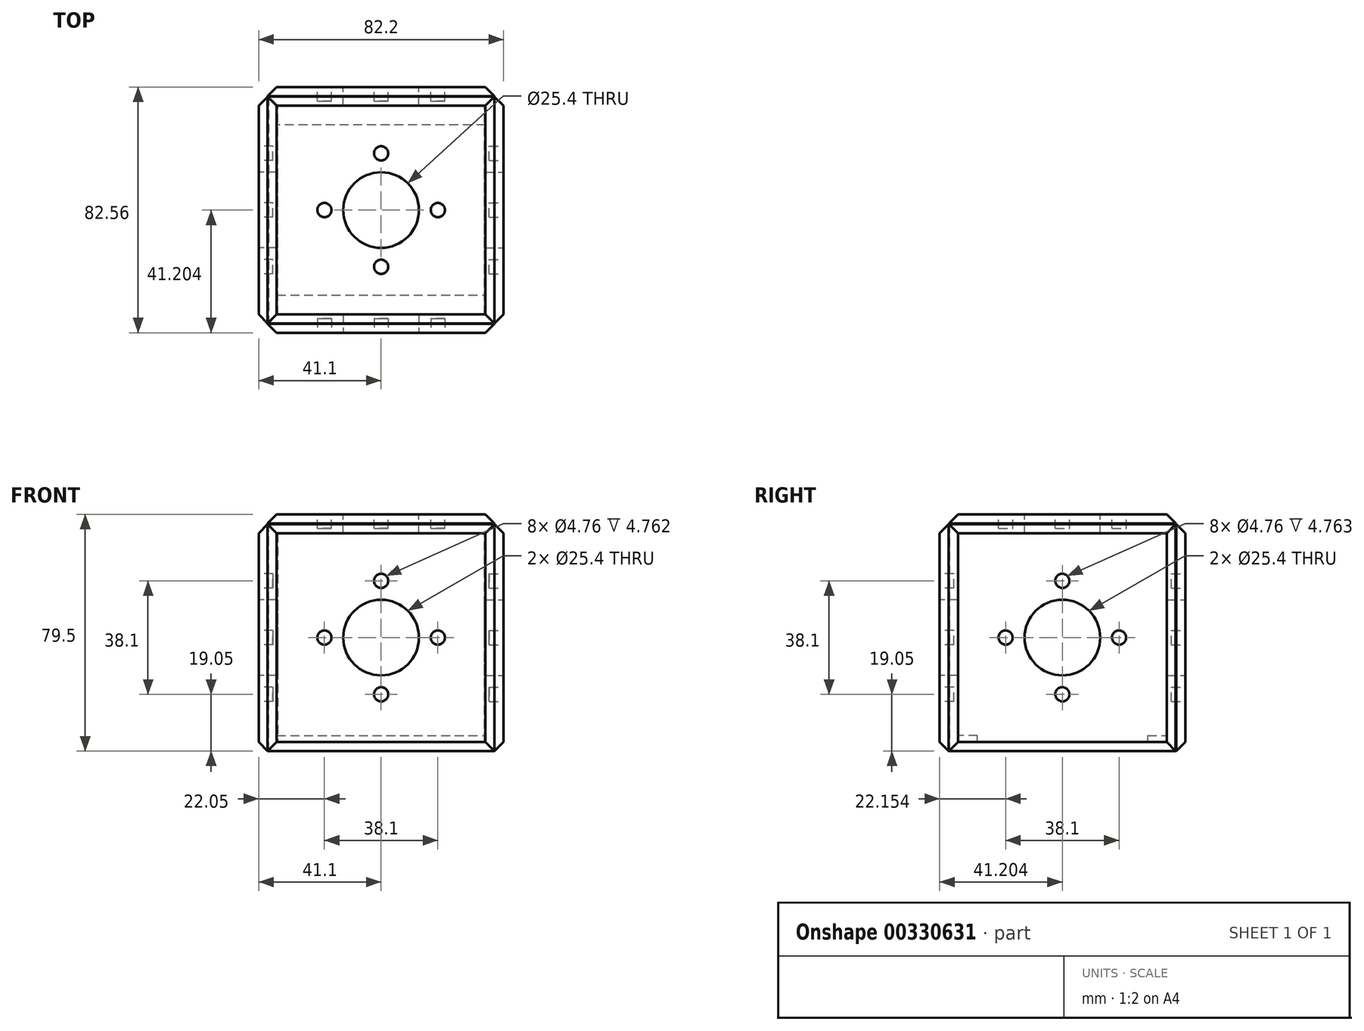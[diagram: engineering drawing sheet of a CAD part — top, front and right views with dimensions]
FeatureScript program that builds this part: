
annotation { "Feature Type Name" : "Feature", "Feature Type Description" : "" }
export const myFeature = defineFeature(function(context is Context, id is Id, definition is map)
    precondition{}
    {
        {
            var Q0;
            Q0=qCreatedBy(makeId("Front.planeOp"),FACE);
            var sketch = newSketch(context, id + "F0", { "sketchPlane" : qUnion([Q0])});
            skLineSegment(sketch, "E0.bottom", {"start": v(-38.1, 38.1) * mm, "end": v(38.1, 38.1) * mm});
            skLineSegment(sketch, "E0.top", {"start": v(-38.1, -38.1) * mm, "end": v(38.1, -38.1) * mm});
            skLineSegment(sketch, "E0.left", {"start": v(-38.1, 38.1) * mm, "end": v(-38.1, -38.1) * mm});
            skLineSegment(sketch, "E0.right", {"start": v(38.1, 38.1) * mm, "end": v(38.1, -38.1) * mm});
            skPoint(sketch, "E0.middle", {"position": v(0, 0) * mm});
            skSolve(sketch);
        }
        {
            var Q0;
            Q0=makeQuery(id+"F0.imprint","IMPRINT",FACE,{"disambiguationData":[TD([[makeQuery(id+"F0.imprint","IMPRINT",EDGE,{"derivedFrom":sQuery(id+"F0.wireOp",EDGE,"E0.bottom")}),-1.0]])]});
            extrude(context, id + "F1", {"entities" : qUnion([Q0]), "depth" : 6.35 * mm});
        }
        {
            var Q0;
            Q0=makeQuery(id+"F1.opExtrude","CAP_EDGE",EDGE,{"disambiguationData":[OSD([sQuery(id+"F0.wireOp",EDGE,"E0.bottom")])],"isStart":false});
            var Q1;
            Q1=makeQuery(id+"F1.opExtrude","CAP_EDGE",EDGE,{"disambiguationData":[OSD([sQuery(id+"F0.wireOp",EDGE,"E0.bottom")])],"isStart":true});
            var Q2;
            Q2=makeQuery(id+"F1.opExtrude","CAP_EDGE",EDGE,{"disambiguationData":[OSD([sQuery(id+"F0.wireOp",EDGE,"E0.left")])],"isStart":false});
            var Q3;
            Q3=makeQuery(id+"F1.opExtrude","CAP_EDGE",EDGE,{"disambiguationData":[OSD([sQuery(id+"F0.wireOp",EDGE,"E0.left")])],"isStart":true});
            var Q4;
            Q4=makeQuery(id+"F1.opExtrude","CAP_EDGE",EDGE,{"disambiguationData":[OSD([sQuery(id+"F0.wireOp",EDGE,"E0.top")])],"isStart":false});
            var Q5;
            Q5=makeQuery(id+"F1.opExtrude","CAP_EDGE",EDGE,{"disambiguationData":[OSD([sQuery(id+"F0.wireOp",EDGE,"E0.top")])],"isStart":true});
            var Q6;
            Q6=makeQuery(id+"F1.opExtrude","CAP_EDGE",EDGE,{"disambiguationData":[OSD([sQuery(id+"F0.wireOp",EDGE,"E0.right")])],"isStart":false});
            var Q7;
            Q7=makeQuery(id+"F1.opExtrude","CAP_EDGE",EDGE,{"disambiguationData":[OSD([sQuery(id+"F0.wireOp",EDGE,"E0.right")])],"isStart":true});
            chamfer(context, id + "F2", {"entities" : qUnion([Q0, Q1, Q2, Q3, Q4, Q5, Q6, Q7]), "chamferType" : ChamferType.OFFSET_ANGLE, "width" : 3.05 * mm, "oppositeDirection" : false, "angle" : 45 * degree, "tangentPropagation" : true});
        }
        {
            var Q0;
            Q0=makeQuery(id+"F1.opExtrude","CAP_FACE",FACE,{"disambiguationData":[OSD([sQuery(id+"F0.wireOp",EDGE,"E0.bottom"),sQuery(id+"F0.wireOp",EDGE,"E0.top"),sQuery(id+"F0.wireOp",EDGE,"E0.left"),sQuery(id+"F0.wireOp",EDGE,"E0.right")])],"isStart":false});
            var sketch = newSketch(context, id + "F3", { "sketchPlane" : qUnion([Q0])});
            skCircle(sketch, "E1", {"center": v(0, 0) * mm, "radius": 12.7 * mm});
            skSolve(sketch);
        }
        {
            var Q0;
            Q0=makeQuery(id+"F3.imprint","IMPRINT",FACE,{"disambiguationData":[TD([[makeQuery(id+"F3.imprint","IMPRINT",EDGE,{"derivedFrom":sQuery(id+"F3.wireOp",EDGE,"E1")}),1.0]])]});
            extrude(context, id + "F4", {"entities" : qUnion([Q0]), "operationType" : NewBodyOperationType.REMOVE, "oppositeDirection" : true, "depth" : 6.35 * mm});
        }
        {
            var Q0;
            Q0=makeQuery(id+"F1.opExtrude","CAP_FACE",FACE,{"disambiguationData":[OSD([sQuery(id+"F0.wireOp",EDGE,"E0.bottom"),sQuery(id+"F0.wireOp",EDGE,"E0.top"),sQuery(id+"F0.wireOp",EDGE,"E0.left"),sQuery(id+"F0.wireOp",EDGE,"E0.right")])],"isStart":false});
            var sketch = newSketch(context, id + "F5", { "sketchPlane" : qUnion([Q0])});
            skCircle(sketch, "E2", {"center": v(0, 19.05) * mm, "radius": 2.38 * mm});
            skCircle(sketch, "E3.1.0", {"center": v(19.05, 0) * mm, "radius": 2.38 * mm});
            skCircle(sketch, "E3.2.0", {"center": v(0, -19.05) * mm, "radius": 2.38 * mm});
            skCircle(sketch, "E3.3.0", {"center": v(-19.05, 0) * mm, "radius": 2.38 * mm});
            skPoint(sketch, "E3.center", {"position": v(0, 0) * mm});
            skLineSegment(sketch, "E3.anchor1", {"start": v(0, 0) * mm, "end": v(0, 19.05) * mm, "construction": true});
            skLineSegment(sketch, "E3.anchor2", {"start": v(0, 0) * mm, "end": v(-19.05, 0) * mm, "construction": true});
            skSolve(sketch);
        }
        {
            var Q0;
            Q0=makeQuery(id+"F5.imprint","IMPRINT",FACE,{"disambiguationData":[TD([[makeQuery(id+"F5.imprint","IMPRINT",EDGE,{"derivedFrom":sQuery(id+"F5.wireOp",EDGE,"E2")}),1.0]])]});
            var Q1;
            Q1=makeQuery(id+"F5.imprint","IMPRINT",FACE,{"disambiguationData":[TD([[makeQuery(id+"F5.imprint","IMPRINT",EDGE,{"derivedFrom":sQuery(id+"F5.wireOp",EDGE,"E3.1.0")}),1.0]])]});
            var Q2;
            Q2=makeQuery(id+"F5.imprint","IMPRINT",FACE,{"disambiguationData":[TD([[makeQuery(id+"F5.imprint","IMPRINT",EDGE,{"derivedFrom":sQuery(id+"F5.wireOp",EDGE,"E3.2.0")}),1.0]])]});
            var Q3;
            Q3=makeQuery(id+"F5.imprint","IMPRINT",FACE,{"disambiguationData":[TD([[makeQuery(id+"F5.imprint","IMPRINT",EDGE,{"derivedFrom":sQuery(id+"F5.wireOp",EDGE,"E3.3.0")}),1.0]])]});
            extrude(context, id + "F6", {"entities" : qUnion([Q0, Q1, Q2, Q3]), "operationType" : NewBodyOperationType.REMOVE, "oppositeDirection" : true, "depth" : 4.76 * mm});
        }
        {
            var Q0;
            Q0=makeQuery(id+"F1.opExtrude","SWEPT_BODY",BODY,{"disambiguationData":[OSD([sQuery(id+"F0.wireOp",EDGE,"E0.bottom"),sQuery(id+"F0.wireOp",EDGE,"E0.top"),sQuery(id+"F0.wireOp",EDGE,"E0.left"),sQuery(id+"F0.wireOp",EDGE,"E0.right")])]});
            transform(context, id + "F7", {"entities" : qUnion([Q0]), "transformType" : TransformType.TRANSLATION_3D, "dx" : 0 * mm, "dy" : -34.92 * mm, "dz" : 0 * mm, "makeCopy" : false});
        }
        {
            var Q0;
            Q0=makeQuery(id+"F1.opExtrude","SWEPT_BODY",BODY,{"disambiguationData":[OSD([sQuery(id+"F0.wireOp",EDGE,"E0.bottom"),sQuery(id+"F0.wireOp",EDGE,"E0.top"),sQuery(id+"F0.wireOp",EDGE,"E0.left"),sQuery(id+"F0.wireOp",EDGE,"E0.right")])]});
            var Q1;
            Q1=qCreatedBy(makeId("Front.planeOp"),FACE);
            mirror(context, id + "F8", {"entities" : qUnion([Q0]), "mirrorPlane" : qUnion([Q1])});
        }
        {
            var Q0;
            Q0=makeQuery(id+"F8.opPattern","COPY",FACE,{"derivedFrom":makeQuery(id+"F1.opExtrude","SWEPT_FACE",FACE,{"disambiguationData":[OSD([sQuery(id+"F0.wireOp",EDGE,"E0.bottom")])]}),"instanceName":"1"});
            cPlane(context, id + "F9", {"entities" : qUnion([Q0]), "cplaneType" : CPlaneType.OFFSET, "offset" : 1.78 * mm, "width" : 152.4 * mm, "height" : 152.4 * mm});
        }
        {
            var Q0;
            Q0=makeQuery(id+"F8.opPattern","COPY",BODY,{"derivedFrom":makeQuery(id+"F1.opExtrude","SWEPT_BODY",BODY,{"disambiguationData":[OSD([sQuery(id+"F0.wireOp",EDGE,"E0.bottom"),sQuery(id+"F0.wireOp",EDGE,"E0.top"),sQuery(id+"F0.wireOp",EDGE,"E0.left"),sQuery(id+"F0.wireOp",EDGE,"E0.right")])]}),"instanceName":"1"});
            var Q1;
            Q1=qCreatedBy(id+"F9.planeOp",FACE);
            mirror(context, id + "F10", {"operationType" : NewBodyOperationType.ADD, "entities" : qUnion([Q0]), "mirrorPlane" : qUnion([Q1])});
        }
        {
            var Q0;
            Q0=makeQuery(id+"F10.opPattern","COPY",BODY,{"derivedFrom":makeQuery(id+"F8.opPattern","COPY",BODY,{"derivedFrom":makeQuery(id+"F1.opExtrude","SWEPT_BODY",BODY,{"disambiguationData":[OSD([sQuery(id+"F0.wireOp",EDGE,"E0.bottom"),sQuery(id+"F0.wireOp",EDGE,"E0.top"),sQuery(id+"F0.wireOp",EDGE,"E0.left"),sQuery(id+"F0.wireOp",EDGE,"E0.right")])]}),"instanceName":"1"}),"instanceName":"1"});
            var Q1;
            {var subQ0=sQuery(id+"F0.wireOp",EDGE,"E0.bottom");Q1=makeQuery(id+"F8.opPattern","COPY",EDGE,{"derivedFrom":makeQuery(id+"F2.opChamfer","BLEND_EDGE",EDGE,{"blendedFrom":[makeQuery(id+"F1.opExtrude","CAP_EDGE",EDGE,{"disambiguationData":[OSD([subQ0])],"isStart":true}),makeQuery(id+"F1.opExtrude","SWEPT_FACE",FACE,{"disambiguationData":[OSD([subQ0])]})],"blendedInto":[makeQuery(id+"F1.opExtrude","SWEPT_FACE",FACE,{"disambiguationData":[OSD([subQ0])]})]}),"instanceName":"1"});}
            transform(context, id + "F11", {"entities" : qUnion([Q0]), "transformType" : TransformType.ROTATION, "transformAxis" : qUnion([Q1]), "angle" : 90 * degree, "oppositeDirection" : true, "makeCopy" : false});
        }
        {
            var Q0;
            Q0=makeQuery(id+"F10.opPattern","COPY",BODY,{"derivedFrom":makeQuery(id+"F8.opPattern","COPY",BODY,{"derivedFrom":makeQuery(id+"F1.opExtrude","SWEPT_BODY",BODY,{"disambiguationData":[OSD([sQuery(id+"F0.wireOp",EDGE,"E0.bottom"),sQuery(id+"F0.wireOp",EDGE,"E0.top"),sQuery(id+"F0.wireOp",EDGE,"E0.left"),sQuery(id+"F0.wireOp",EDGE,"E0.right")])]}),"instanceName":"1"}),"instanceName":"1"});
            transform(context, id + "F12", {"entities" : qUnion([Q0]), "transformType" : TransformType.TRANSLATION_3D, "dx" : 0 * mm, "dy" : 3.6 * mm, "dz" : 0 * mm, "makeCopy" : false});
        }
        {
            var Q0;
            Q0=makeQuery(id+"F10.opPattern","COPY",FACE,{"derivedFrom":makeQuery(id+"F8.opPattern","COPY",FACE,{"derivedFrom":makeQuery(id+"F1.opExtrude","SWEPT_FACE",FACE,{"disambiguationData":[OSD([sQuery(id+"F0.wireOp",EDGE,"E0.right")])]}),"instanceName":"1"}),"instanceName":"1"});
            cPlane(context, id + "F13", {"entities" : qUnion([Q0]), "cplaneType" : CPlaneType.OFFSET, "offset" : 0.36 * mm, "width" : 152.4 * mm, "height" : 152.4 * mm});
        }
        {
            var Q0;
            Q0=makeQuery(id+"F10.opPattern","COPY",BODY,{"derivedFrom":makeQuery(id+"F8.opPattern","COPY",BODY,{"derivedFrom":makeQuery(id+"F1.opExtrude","SWEPT_BODY",BODY,{"disambiguationData":[OSD([sQuery(id+"F0.wireOp",EDGE,"E0.bottom"),sQuery(id+"F0.wireOp",EDGE,"E0.top"),sQuery(id+"F0.wireOp",EDGE,"E0.left"),sQuery(id+"F0.wireOp",EDGE,"E0.right")])]}),"instanceName":"1"}),"instanceName":"1"});
            var Q1;
            Q1=qCreatedBy(id+"F13.planeOp",FACE);
            mirror(context, id + "F14", {"entities" : qUnion([Q0]), "mirrorPlane" : qUnion([Q1])});
        }
        {
            var Q0;
            Q0=makeQuery(id+"F14.opPattern","COPY",BODY,{"derivedFrom":makeQuery(id+"F10.opPattern","COPY",BODY,{"derivedFrom":makeQuery(id+"F8.opPattern","COPY",BODY,{"derivedFrom":makeQuery(id+"F1.opExtrude","SWEPT_BODY",BODY,{"disambiguationData":[OSD([sQuery(id+"F0.wireOp",EDGE,"E0.bottom"),sQuery(id+"F0.wireOp",EDGE,"E0.top"),sQuery(id+"F0.wireOp",EDGE,"E0.left"),sQuery(id+"F0.wireOp",EDGE,"E0.right")])]}),"instanceName":"1"}),"instanceName":"1"}),"instanceName":"1"});
            var Q1;
            {var subQ0=sQuery(id+"F0.wireOp",EDGE,"E0.right");Q1=makeQuery(id+"F14.opPattern","COPY",EDGE,{"derivedFrom":makeQuery(id+"F10.opPattern","COPY",EDGE,{"derivedFrom":makeQuery(id+"F8.opPattern","COPY",EDGE,{"derivedFrom":makeQuery(id+"F2.opChamfer","BLEND_EDGE",EDGE,{"blendedFrom":[makeQuery(id+"F1.opExtrude","CAP_EDGE",EDGE,{"disambiguationData":[OSD([subQ0])],"isStart":false}),makeQuery(id+"F1.opExtrude","SWEPT_FACE",FACE,{"disambiguationData":[OSD([subQ0])]})],"blendedInto":[makeQuery(id+"F1.opExtrude","SWEPT_FACE",FACE,{"disambiguationData":[OSD([subQ0])]})]}),"instanceName":"1"}),"instanceName":"1"}),"instanceName":"1"});}
            transform(context, id + "F15", {"entities" : qUnion([Q0]), "transformType" : TransformType.ROTATION, "transformAxis" : qUnion([Q1]), "angle" : 90 * degree, "oppositeDirection" : true, "makeCopy" : false});
        }
        {
            var Q0;
            Q0=makeQuery(id+"F14.opPattern","COPY",BODY,{"derivedFrom":makeQuery(id+"F10.opPattern","COPY",BODY,{"derivedFrom":makeQuery(id+"F8.opPattern","COPY",BODY,{"derivedFrom":makeQuery(id+"F1.opExtrude","SWEPT_BODY",BODY,{"disambiguationData":[OSD([sQuery(id+"F0.wireOp",EDGE,"E0.bottom"),sQuery(id+"F0.wireOp",EDGE,"E0.top"),sQuery(id+"F0.wireOp",EDGE,"E0.left"),sQuery(id+"F0.wireOp",EDGE,"E0.right")])]}),"instanceName":"1"}),"instanceName":"1"}),"instanceName":"1"});
            transform(context, id + "F16", {"entities" : qUnion([Q0]), "transformType" : TransformType.TRANSLATION_3D, "dx" : -0.76 * mm, "dy" : 0 * mm, "dz" : 0 * mm, "makeCopy" : false});
        }
        {
            var Q0;
            Q0=makeQuery(id+"F10.opPattern","COPY",FACE,{"derivedFrom":makeQuery(id+"F8.opPattern","COPY",FACE,{"derivedFrom":makeQuery(id+"F1.opExtrude","SWEPT_FACE",FACE,{"disambiguationData":[OSD([sQuery(id+"F0.wireOp",EDGE,"E0.left")])]}),"instanceName":"1"}),"instanceName":"1"});
            cPlane(context, id + "F17", {"entities" : qUnion([Q0]), "cplaneType" : CPlaneType.OFFSET, "offset" : 0.36 * mm, "width" : 152.4 * mm, "height" : 152.4 * mm});
        }
        {
            var Q0;
            Q0=makeQuery(id+"F10.opPattern","COPY",BODY,{"derivedFrom":makeQuery(id+"F8.opPattern","COPY",BODY,{"derivedFrom":makeQuery(id+"F1.opExtrude","SWEPT_BODY",BODY,{"disambiguationData":[OSD([sQuery(id+"F0.wireOp",EDGE,"E0.bottom"),sQuery(id+"F0.wireOp",EDGE,"E0.top"),sQuery(id+"F0.wireOp",EDGE,"E0.left"),sQuery(id+"F0.wireOp",EDGE,"E0.right")])]}),"instanceName":"1"}),"instanceName":"1"});
            var Q1;
            Q1=qCreatedBy(id+"F17.planeOp",FACE);
            mirror(context, id + "F18", {"entities" : qUnion([Q0]), "mirrorPlane" : qUnion([Q1])});
        }
        {
            var Q0;
            Q0=makeQuery(id+"F18.opPattern","COPY",BODY,{"derivedFrom":makeQuery(id+"F10.opPattern","COPY",BODY,{"derivedFrom":makeQuery(id+"F8.opPattern","COPY",BODY,{"derivedFrom":makeQuery(id+"F1.opExtrude","SWEPT_BODY",BODY,{"disambiguationData":[OSD([sQuery(id+"F0.wireOp",EDGE,"E0.bottom"),sQuery(id+"F0.wireOp",EDGE,"E0.top"),sQuery(id+"F0.wireOp",EDGE,"E0.left"),sQuery(id+"F0.wireOp",EDGE,"E0.right")])]}),"instanceName":"1"}),"instanceName":"1"}),"instanceName":"1"});
            var Q1;
            {var subQ0=sQuery(id+"F0.wireOp",EDGE,"E0.left");Q1=makeQuery(id+"F18.opPattern","COPY",EDGE,{"derivedFrom":makeQuery(id+"F10.opPattern","COPY",EDGE,{"derivedFrom":makeQuery(id+"F8.opPattern","COPY",EDGE,{"derivedFrom":makeQuery(id+"F2.opChamfer","BLEND_EDGE",EDGE,{"blendedFrom":[makeQuery(id+"F1.opExtrude","CAP_EDGE",EDGE,{"disambiguationData":[OSD([subQ0])],"isStart":false}),makeQuery(id+"F1.opExtrude","SWEPT_FACE",FACE,{"disambiguationData":[OSD([subQ0])]})],"blendedInto":[makeQuery(id+"F1.opExtrude","SWEPT_FACE",FACE,{"disambiguationData":[OSD([subQ0])]})]}),"instanceName":"1"}),"instanceName":"1"}),"instanceName":"1"});}
            transform(context, id + "F19", {"entities" : qUnion([Q0]), "transformType" : TransformType.ROTATION, "transformAxis" : qUnion([Q1]), "angle" : 90 * degree, "oppositeDirection" : true, "makeCopy" : false});
        }
        {
            var Q0;
            Q0=makeQuery(id+"F18.opPattern","COPY",BODY,{"derivedFrom":makeQuery(id+"F10.opPattern","COPY",BODY,{"derivedFrom":makeQuery(id+"F8.opPattern","COPY",BODY,{"derivedFrom":makeQuery(id+"F1.opExtrude","SWEPT_BODY",BODY,{"disambiguationData":[OSD([sQuery(id+"F0.wireOp",EDGE,"E0.bottom"),sQuery(id+"F0.wireOp",EDGE,"E0.top"),sQuery(id+"F0.wireOp",EDGE,"E0.left"),sQuery(id+"F0.wireOp",EDGE,"E0.right")])]}),"instanceName":"1"}),"instanceName":"1"}),"instanceName":"1"});
            transform(context, id + "F20", {"entities" : qUnion([Q0]), "transformType" : TransformType.TRANSLATION_3D, "dx" : 0.76 * mm, "dy" : 0 * mm, "dz" : 0 * mm, "makeCopy" : false});
        }
        {
            var Q0;
            Q0=makeQuery(id+"F14.opPattern","COPY",BODY,{"derivedFrom":makeQuery(id+"F10.opPattern","COPY",BODY,{"derivedFrom":makeQuery(id+"F8.opPattern","COPY",BODY,{"derivedFrom":makeQuery(id+"F1.opExtrude","SWEPT_BODY",BODY,{"disambiguationData":[OSD([sQuery(id+"F0.wireOp",EDGE,"E0.bottom"),sQuery(id+"F0.wireOp",EDGE,"E0.top"),sQuery(id+"F0.wireOp",EDGE,"E0.left"),sQuery(id+"F0.wireOp",EDGE,"E0.right")])]}),"instanceName":"1"}),"instanceName":"1"}),"instanceName":"1"});
            transform(context, id + "F21", {"entities" : qUnion([Q0]), "transformType" : TransformType.TRANSLATION_3D, "dx" : 0 * mm, "dy" : 0 * mm, "dz" : -0.25 * mm, "makeCopy" : false});
        }
        {
            var Q0;
            Q0=makeQuery(id+"F18.opPattern","COPY",BODY,{"derivedFrom":makeQuery(id+"F10.opPattern","COPY",BODY,{"derivedFrom":makeQuery(id+"F8.opPattern","COPY",BODY,{"derivedFrom":makeQuery(id+"F1.opExtrude","SWEPT_BODY",BODY,{"disambiguationData":[OSD([sQuery(id+"F0.wireOp",EDGE,"E0.bottom"),sQuery(id+"F0.wireOp",EDGE,"E0.top"),sQuery(id+"F0.wireOp",EDGE,"E0.left"),sQuery(id+"F0.wireOp",EDGE,"E0.right")])]}),"instanceName":"1"}),"instanceName":"1"}),"instanceName":"1"});
            transform(context, id + "F22", {"entities" : qUnion([Q0]), "transformType" : TransformType.TRANSLATION_3D, "dx" : 0 * mm, "dy" : 0 * mm, "dz" : -0.25 * mm, "makeCopy" : false});
        }
        {
            var Q0;
            Q0=makeQuery(id+"F1.opExtrude","CAP_FACE",FACE,{"disambiguationData":[OSD([sQuery(id+"F0.wireOp",EDGE,"E0.bottom"),sQuery(id+"F0.wireOp",EDGE,"E0.top"),sQuery(id+"F0.wireOp",EDGE,"E0.left"),sQuery(id+"F0.wireOp",EDGE,"E0.right")])],"isStart":true});
            var sketch = newSketch(context, id + "F23", { "sketchPlane" : qUnion([Q0])});
            skLineSegment(sketch, "E4.bottom", {"start": v(35.05, -35.05) * mm, "end": v(-35.05, -35.05) * mm});
            skLineSegment(sketch, "E4.top", {"start": v(35.05, -32.85) * mm, "end": v(-35.05, -32.85) * mm});
            skLineSegment(sketch, "E4.left", {"start": v(35.05, -35.05) * mm, "end": v(35.05, -32.85) * mm});
            skLineSegment(sketch, "E4.right", {"start": v(-35.05, -35.05) * mm, "end": v(-35.05, -32.85) * mm});
            skSolve(sketch);
        }
        {
            var Q0;
            Q0=makeQuery(id+"F23.imprint","IMPRINT",FACE,{"disambiguationData":[TD([[makeQuery(id+"F23.imprint","IMPRINT",EDGE,{"derivedFrom":sQuery(id+"F23.wireOp",EDGE,"E4.bottom")}),1.0]])]});
            extrude(context, id + "F24", {"entities" : qUnion([Q0]), "depth" : 6.35 * mm});
        }
        {
            var Q0;
            Q0=makeQuery(id+"F8.opPattern","COPY",FACE,{"derivedFrom":makeQuery(id+"F1.opExtrude","CAP_FACE",FACE,{"disambiguationData":[OSD([sQuery(id+"F0.wireOp",EDGE,"E0.bottom"),sQuery(id+"F0.wireOp",EDGE,"E0.top"),sQuery(id+"F0.wireOp",EDGE,"E0.left"),sQuery(id+"F0.wireOp",EDGE,"E0.right")])],"isStart":true}),"instanceName":"1"});
            var sketch = newSketch(context, id + "F25", { "sketchPlane" : qUnion([Q0])});
            skLineSegment(sketch, "E5.bottom", {"start": v(35.05, -35.05) * mm, "end": v(-35.05, -35.05) * mm});
            skLineSegment(sketch, "E5.top", {"start": v(35.05, -32.85) * mm, "end": v(-35.05, -32.85) * mm});
            skLineSegment(sketch, "E5.left", {"start": v(35.05, -35.05) * mm, "end": v(35.05, -32.85) * mm});
            skLineSegment(sketch, "E5.right", {"start": v(-35.05, -35.05) * mm, "end": v(-35.05, -32.85) * mm});
            skSolve(sketch);
        }
        {
            var Q0;
            Q0=makeQuery(id+"F25.imprint","IMPRINT",FACE,{"disambiguationData":[TD([[makeQuery(id+"F25.imprint","IMPRINT",EDGE,{"derivedFrom":sQuery(id+"F25.wireOp",EDGE,"E5.bottom")}),-1.0]])]});
            extrude(context, id + "F26", {"entities" : qUnion([Q0]), "depth" : 6.35 * mm});
        }
    });
